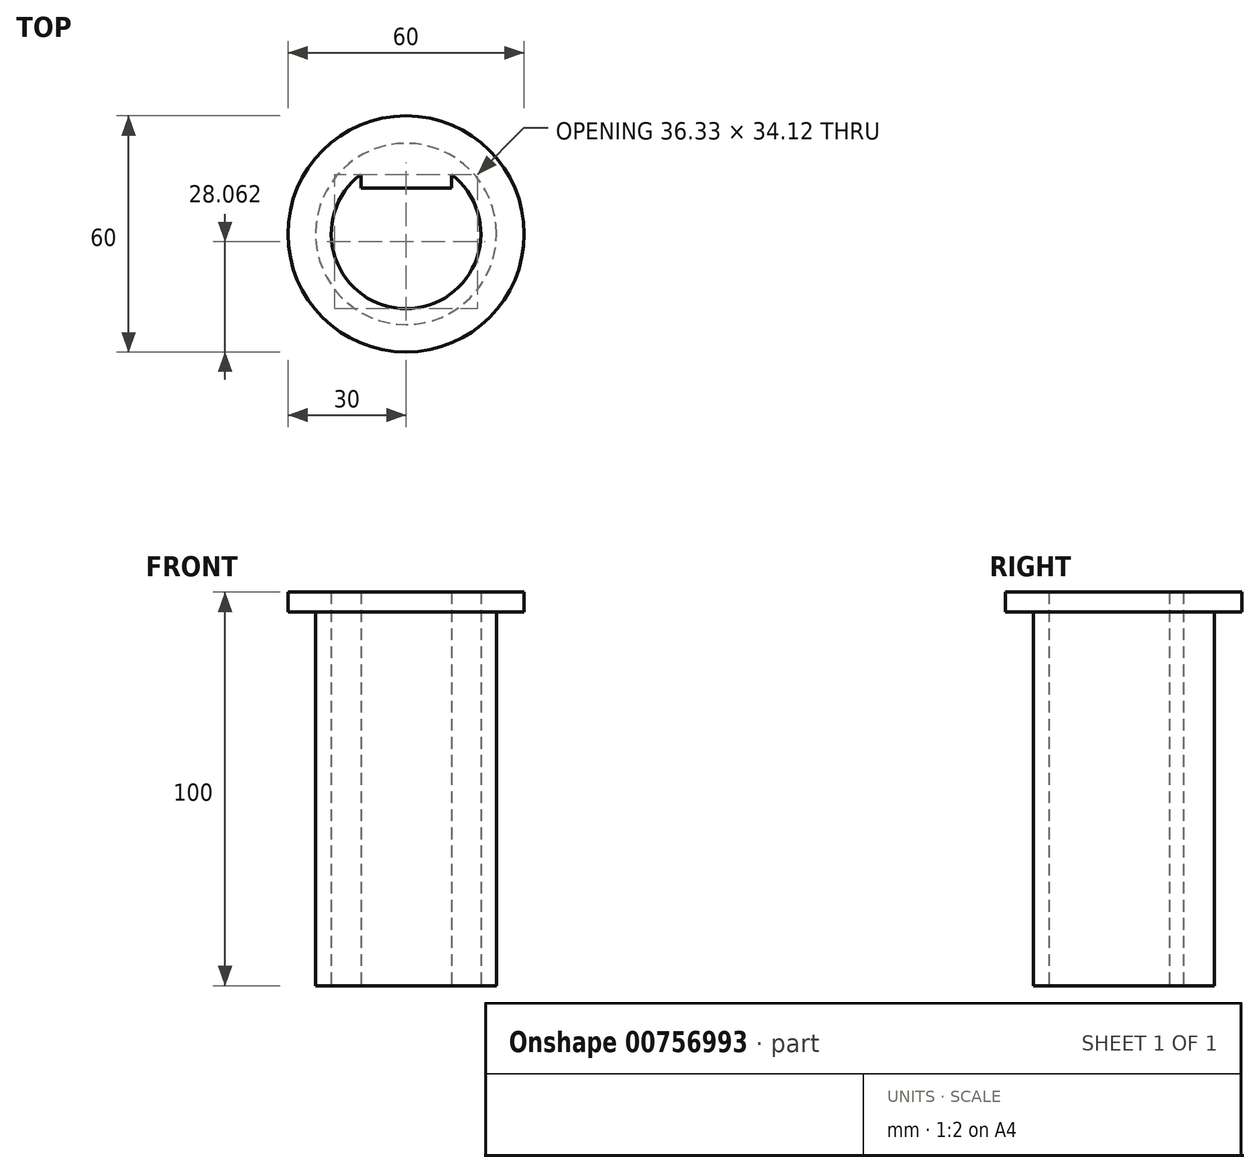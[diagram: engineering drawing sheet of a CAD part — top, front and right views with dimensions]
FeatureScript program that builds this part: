
annotation { "Feature Type Name" : "Feature", "Feature Type Description" : "" }
export const myFeature = defineFeature(function(context is Context, id is Id, definition is map)
    precondition{}
    {
        {
            var Q0;
            Q0=qCreatedBy(makeId("Top.planeOp"),FACE);
            var sketch = newSketch(context, id + "F0", { "sketchPlane" : qUnion([Q0])});
            skCircle(sketch, "E0", {"center": v(0, 0) * mm, "radius": 23 * mm});
            skArc(sketch, "E1", {"start": v(-11.5, 15.12) * mm, "mid": v(0, -19) * mm, "end": v(11.5, 15.12) * mm});
            skLineSegment(sketch, "E2", {"start": v(-11.5, 15.12) * mm, "end": v(-11.5, 11.6) * mm});
            skLineSegment(sketch, "E3", {"start": v(-11.5, 11.6) * mm, "end": v(11.5, 11.6) * mm});
            skLineSegment(sketch, "E4", {"start": v(11.5, 11.6) * mm, "end": v(11.5, 15.12) * mm});
            skSolve(sketch);
        }
        {
            var Q0;
            Q0=makeQuery(id+"F0.imprint","IMPRINT",FACE,{"disambiguationData":[TD([[makeQuery(id+"F0.imprint","IMPRINT",EDGE,{"derivedFrom":sQuery(id+"F0.wireOp",EDGE,"E0")}),1.0]])]});
            extrude(context, id + "F1", {"entities" : qUnion([Q0]), "depth" : 100 * mm, "offsetDistance" : 25 * mm});
        }
        {
            var Q0;
            Q0=makeQuery(id+"F1.opExtrude","CAP_FACE",FACE,{"disambiguationData":[OSD([sQuery(id+"F0.wireOp",EDGE,"E0"),sQuery(id+"F0.wireOp",EDGE,"E1"),sQuery(id+"F0.wireOp",EDGE,"E2"),sQuery(id+"F0.wireOp",EDGE,"E3"),sQuery(id+"F0.wireOp",EDGE,"E4")])],"isStart":false});
            var sketch = newSketch(context, id + "F2", { "sketchPlane" : qUnion([Q0])});
            skCircle(sketch, "E5", {"center": v(0, 0) * mm, "radius": 23 * mm});
            skCircle(sketch, "E6", {"center": v(0, 0) * mm, "radius": 30 * mm});
            skSolve(sketch);
        }
        {
            var Q0;
            Q0=makeQuery(id+"F2.imprint","IMPRINT",FACE,{"disambiguationData":[TD([[makeQuery(id+"F2.imprint","IMPRINT",EDGE,{"derivedFrom":sQuery(id+"F2.wireOp",EDGE,"E6")}),1.0]])]});
            extrude(context, id + "F3", {"entities" : qUnion([Q0]), "operationType" : NewBodyOperationType.ADD, "oppositeDirection" : true, "depth" : 5 * mm, "offsetDistance" : 25 * mm});
        }
    });
